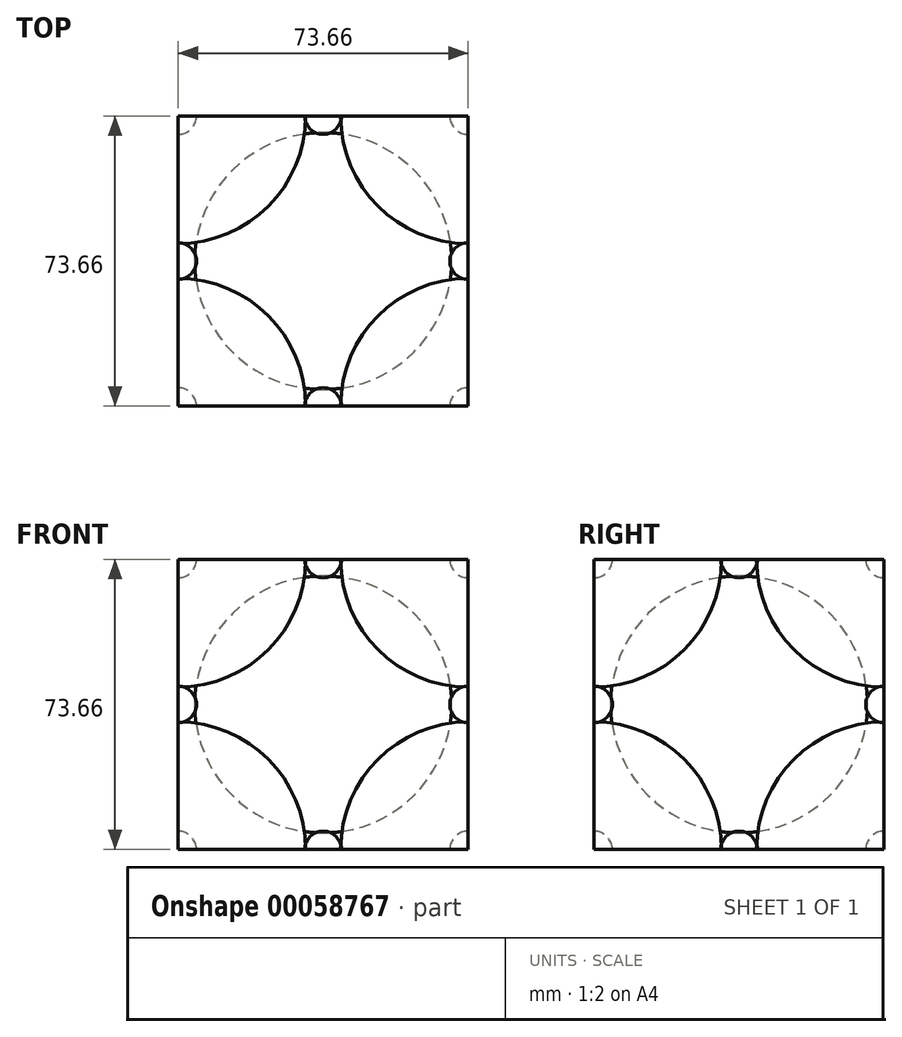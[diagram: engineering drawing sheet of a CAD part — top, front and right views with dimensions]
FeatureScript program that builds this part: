
annotation { "Feature Type Name" : "Feature", "Feature Type Description" : "" }
export const myFeature = defineFeature(function(context is Context, id is Id, definition is map)
    precondition{}
    {
        {
            var Q0;
            Q0=qCreatedBy(makeId("Top.planeOp"),FACE);
            var sketch = newSketch(context, id + "F0", { "sketchPlane" : qUnion([Q0])});
            skLineSegment(sketch, "E0.rect.bottom", {"start": v(36.83, 36.83) * mm, "end": v(-36.83, 36.83) * mm, "construction": true});
            skLineSegment(sketch, "E0.rect.top", {"start": v(36.83, -36.83) * mm, "end": v(-36.83, -36.83) * mm, "construction": true});
            skLineSegment(sketch, "E0.rect.left", {"start": v(36.83, 36.83) * mm, "end": v(36.83, -36.83) * mm, "construction": true});
            skLineSegment(sketch, "E0.rect.right", {"start": v(-36.83, 36.83) * mm, "end": v(-36.83, -36.83) * mm, "construction": true});
            skPoint(sketch, "E0.rect.middle", {"position": v(0, 0) * mm});
            skArc(sketch, "E1", {"start": v(-36.83, 4.44) * mm, "mid": v(-13.93, 13.93) * mm, "end": v(-4.45, 36.83) * mm});
            skLineSegment(sketch, "E2", {"start": v(-36.83, 4.44) * mm, "end": v(-36.83, 36.83) * mm});
            skLineSegment(sketch, "E3", {"start": v(-36.83, 36.83) * mm, "end": v(-4.45, 36.83) * mm});
            skSolve(sketch);
        }
        {
            var Q0;
            Q0=makeQuery(id+"F0.imprint","IMPRINT",FACE,{"disambiguationData":[TD([[makeQuery(id+"F0.imprint","IMPRINT",EDGE,{"derivedFrom":sQuery(id+"F0.wireOp",EDGE,"E1")}),1.0]])]});
            var Q1;
            Q1=sQuery(id+"F0.wireOp",EDGE,"E2");
            revolve(context, id + "F1", {"entities" : qUnion([Q0]), "axis" : qUnion([Q1]), "revolveType" : RevolveType.ONE_DIRECTION, "oppositeDirection" : true, "angle" : 90 * degree});
        }
        {
            var Q0;
            Q0=qCreatedBy(makeId("Front.planeOp"),FACE);
            var sketch = newSketch(context, id + "F2", { "sketchPlane" : qUnion([Q0])});
            skLineSegment(sketch, "E4", {"start": v(0, 0) * mm, "end": v(0, 25.4) * mm, "construction": true});
            skSolve(sketch);
        }
        {
            var Q0;
            Q0=makeQuery(id+"F1.opRevolve","SWEPT_BODY",BODY,{"disambiguationData":[OSD([sQuery(id+"F0.wireOp",EDGE,"E1"),sQuery(id+"F0.wireOp",EDGE,"E2"),sQuery(id+"F0.wireOp",EDGE,"E3")])]});
            var Q1;
            Q1=sQuery(id+"F2.wireOp",EDGE,"E4");
            circularPattern(context, id + "F3", {"entities" : qUnion([Q0]), "axis" : qUnion([Q1]), "angle" : 90 * degree, "instanceCount" : 4});
        }
        {
            var Q0;
            Q0=qCreatedBy(makeId("Top.planeOp"),FACE);
            cPlane(context, id + "F4", {"entities" : qUnion([Q0]), "cplaneType" : CPlaneType.OFFSET, "offset" : 36.83 * mm, "width" : 152.4 * mm, "height" : 152.4 * mm});
        }
        {
            var Q0;
            Q0=makeQuery(id+"F1.opRevolve","SWEPT_BODY",BODY,{"disambiguationData":[OSD([sQuery(id+"F0.wireOp",EDGE,"E1"),sQuery(id+"F0.wireOp",EDGE,"E2"),sQuery(id+"F0.wireOp",EDGE,"E3")])]});
            var Q1;
            Q1=makeQuery(id+"F3.opPattern","COPY",BODY,{"derivedFrom":makeQuery(id+"F1.opRevolve","SWEPT_BODY",BODY,{"disambiguationData":[OSD([sQuery(id+"F0.wireOp",EDGE,"E1"),sQuery(id+"F0.wireOp",EDGE,"E2"),sQuery(id+"F0.wireOp",EDGE,"E3")])]}),"instanceName":"1"});
            var Q2;
            Q2=makeQuery(id+"F3.opPattern","COPY",BODY,{"derivedFrom":makeQuery(id+"F1.opRevolve","SWEPT_BODY",BODY,{"disambiguationData":[OSD([sQuery(id+"F0.wireOp",EDGE,"E1"),sQuery(id+"F0.wireOp",EDGE,"E2"),sQuery(id+"F0.wireOp",EDGE,"E3")])]}),"instanceName":"2"});
            var Q3;
            Q3=makeQuery(id+"F3.opPattern","COPY",BODY,{"derivedFrom":makeQuery(id+"F1.opRevolve","SWEPT_BODY",BODY,{"disambiguationData":[OSD([sQuery(id+"F0.wireOp",EDGE,"E1"),sQuery(id+"F0.wireOp",EDGE,"E2"),sQuery(id+"F0.wireOp",EDGE,"E3")])]}),"instanceName":"3"});
            var Q4;
            Q4=qCreatedBy(id+"F4.planeOp",FACE);
            mirror(context, id + "F5", {"entities" : qUnion([Q0, Q1, Q2, Q3]), "mirrorPlane" : qUnion([Q4])});
        }
        {
            var Q0;
            Q0=qCreatedBy(id+"F4.planeOp",FACE);
            var sketch = newSketch(context, id + "F6", { "sketchPlane" : qUnion([Q0])});
            skArc(sketch, "E5", {"start": v(-32.64, 0) * mm, "mid": v(0, -32.64) * mm, "end": v(32.64, 0) * mm});
            skLineSegment(sketch, "E6", {"start": v(-32.64, 0) * mm, "end": v(32.64, 0) * mm});
            skSolve(sketch);
        }
        {
            var Q0;
            Q0=makeQuery(id+"F6.imprint","IMPRINT",FACE,{"disambiguationData":[TD([[makeQuery(id+"F6.imprint","IMPRINT",EDGE,{"derivedFrom":sQuery(id+"F6.wireOp",EDGE,"E5")}),1.0]])]});
            var Q1;
            Q1=sQuery(id+"F6.wireOp",EDGE,"E6");
            revolve(context, id + "F7", {"entities" : qUnion([Q0]), "axis" : qUnion([Q1]), "revolveType" : RevolveType.FULL});
        }
        {
            var Q0;
            Q0=qCreatedBy(makeId("Top.planeOp"),FACE);
            var sketch = newSketch(context, id + "F8", { "sketchPlane" : qUnion([Q0])});
            skLineSegment(sketch, "E7", {"start": v(0, 0) * mm, "end": v(0, 36.83) * mm, "construction": true});
            skArc(sketch, "E8", {"start": v(-4.64, 36.83) * mm, "mid": v(0, 32.2) * mm, "end": v(4.64, 36.83) * mm});
            skLineSegment(sketch, "E9", {"start": v(-4.64, 36.83) * mm, "end": v(4.64, 36.83) * mm});
            skSolve(sketch);
        }
        {
            var Q0;
            Q0=makeQuery(id+"F8.imprint","IMPRINT",FACE,{"disambiguationData":[TD([[makeQuery(id+"F8.imprint","IMPRINT",EDGE,{"derivedFrom":sQuery(id+"F8.wireOp",EDGE,"E8")}),1.0]])]});
            var Q1;
            Q1=sQuery(id+"F8.wireOp",EDGE,"E9");
            revolve(context, id + "F9", {"entities" : qUnion([Q0]), "axis" : qUnion([Q1]), "revolveType" : RevolveType.ONE_DIRECTION, "oppositeDirection" : true, "angle" : 90 * degree});
        }
        {
            var Q0;
            Q0=makeQuery(id+"F9.opRevolve","SWEPT_BODY",BODY,{"disambiguationData":[OSD([sQuery(id+"F8.wireOp",EDGE,"E8"),sQuery(id+"F8.wireOp",EDGE,"E9")])]});
            var Q1;
            Q1=sQuery(id+"F2.wireOp",EDGE,"E4");
            circularPattern(context, id + "F10", {"entities" : qUnion([Q0]), "axis" : qUnion([Q1]), "angle" : 90 * degree, "instanceCount" : 4});
        }
        {
            var Q0;
            Q0=makeQuery(id+"F9.opRevolve","SWEPT_BODY",BODY,{"disambiguationData":[OSD([sQuery(id+"F8.wireOp",EDGE,"E8"),sQuery(id+"F8.wireOp",EDGE,"E9")])]});
            var Q1;
            Q1=makeQuery(id+"F10.opPattern","COPY",BODY,{"derivedFrom":makeQuery(id+"F9.opRevolve","SWEPT_BODY",BODY,{"disambiguationData":[OSD([sQuery(id+"F8.wireOp",EDGE,"E8"),sQuery(id+"F8.wireOp",EDGE,"E9")])]}),"instanceName":"3"});
            var Q2;
            Q2=makeQuery(id+"F10.opPattern","COPY",BODY,{"derivedFrom":makeQuery(id+"F9.opRevolve","SWEPT_BODY",BODY,{"disambiguationData":[OSD([sQuery(id+"F8.wireOp",EDGE,"E8"),sQuery(id+"F8.wireOp",EDGE,"E9")])]}),"instanceName":"2"});
            var Q3;
            Q3=makeQuery(id+"F10.opPattern","COPY",BODY,{"derivedFrom":makeQuery(id+"F9.opRevolve","SWEPT_BODY",BODY,{"disambiguationData":[OSD([sQuery(id+"F8.wireOp",EDGE,"E8"),sQuery(id+"F8.wireOp",EDGE,"E9")])]}),"instanceName":"1"});
            var Q4;
            Q4=qCreatedBy(id+"F4.planeOp",FACE);
            mirror(context, id + "F11", {"entities" : qUnion([Q0, Q1, Q2, Q3]), "mirrorPlane" : qUnion([Q4])});
        }
        {
            var Q0;
            Q0=qCreatedBy(id+"F4.planeOp",FACE);
            var sketch = newSketch(context, id + "F12", { "sketchPlane" : qUnion([Q0])});
            skLineSegment(sketch, "E10", {"start": v(0, 0) * mm, "end": v(0, 25.4) * mm, "construction": true});
            skSolve(sketch);
        }
        {
            var Q0;
            Q0=makeQuery(id+"F9.opRevolve","SWEPT_BODY",BODY,{"disambiguationData":[OSD([sQuery(id+"F8.wireOp",EDGE,"E8"),sQuery(id+"F8.wireOp",EDGE,"E9")])]});
            var Q1;
            Q1=makeQuery(id+"F10.opPattern","COPY",BODY,{"derivedFrom":makeQuery(id+"F9.opRevolve","SWEPT_BODY",BODY,{"disambiguationData":[OSD([sQuery(id+"F8.wireOp",EDGE,"E8"),sQuery(id+"F8.wireOp",EDGE,"E9")])]}),"instanceName":"2"});
            var Q2;
            Q2=sQuery(id+"F12.wireOp",EDGE,"E10");
            circularPattern(context, id + "F13", {"entities" : qUnion([Q0, Q1]), "axis" : qUnion([Q2]), "angle" : 90 * degree, "instanceCount" : 2});
        }
        {
            var Q0;
            Q0=makeQuery(id+"F13.opPattern","COPY",BODY,{"derivedFrom":makeQuery(id+"F9.opRevolve","SWEPT_BODY",BODY,{"disambiguationData":[OSD([sQuery(id+"F8.wireOp",EDGE,"E8"),sQuery(id+"F8.wireOp",EDGE,"E9")])]}),"instanceName":"1"});
            var Q1;
            Q1=makeQuery(id+"F13.opPattern","COPY",BODY,{"derivedFrom":makeQuery(id+"F10.opPattern","COPY",BODY,{"derivedFrom":makeQuery(id+"F9.opRevolve","SWEPT_BODY",BODY,{"disambiguationData":[OSD([sQuery(id+"F8.wireOp",EDGE,"E8"),sQuery(id+"F8.wireOp",EDGE,"E9")])]}),"instanceName":"2"}),"instanceName":"1"});
            var Q2;
            Q2=qCreatedBy(makeId("Right.planeOp"),FACE);
            mirror(context, id + "F14", {"entities" : qUnion([Q0, Q1]), "mirrorPlane" : qUnion([Q2])});
        }
    });
